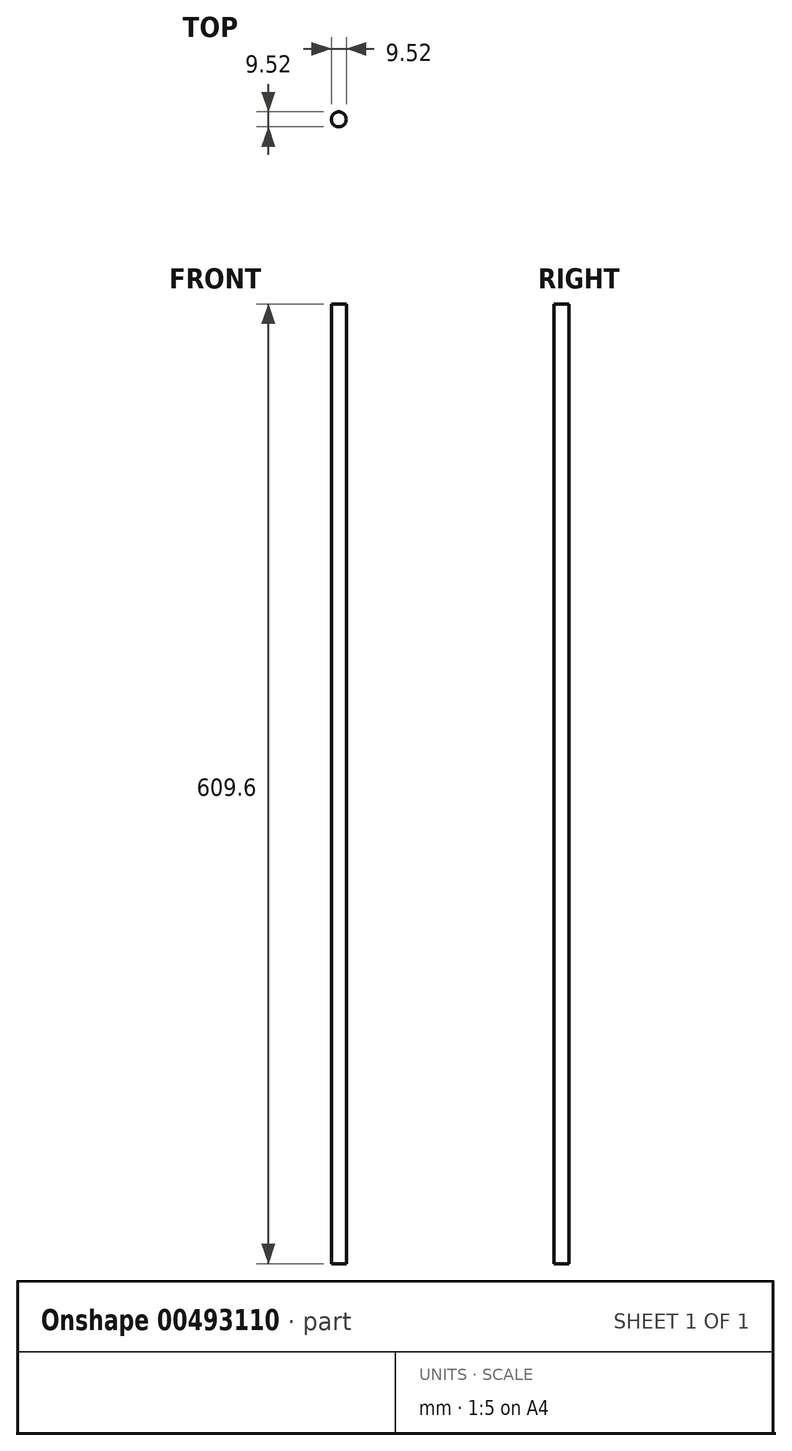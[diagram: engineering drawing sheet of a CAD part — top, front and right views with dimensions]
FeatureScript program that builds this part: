
annotation { "Feature Type Name" : "Feature", "Feature Type Description" : "" }
export const myFeature = defineFeature(function(context is Context, id is Id, definition is map)
    precondition{}
    {
        {
            var Q0;
            Q0=qCreatedBy(makeId("Top.planeOp"),FACE);
            var sketch = newSketch(context, id + "F0", { "sketchPlane" : qUnion([Q0])});
            skCircle(sketch, "E0", {"center": v(0, 0) * mm, "radius": 4.76 * mm});
            skSolve(sketch);
        }
        {
            var Q0;
            Q0=makeQuery(id+"F0.imprint","IMPRINT",FACE,{"disambiguationData":[TD([[makeQuery(id+"F0.imprint","IMPRINT",EDGE,{"derivedFrom":sQuery(id+"F0.wireOp",EDGE,"E0")}),1.0]])]});
            extrude(context, id + "F1", {"entities" : qUnion([Q0]), "depth" : 609.6 * mm});
        }
    });
